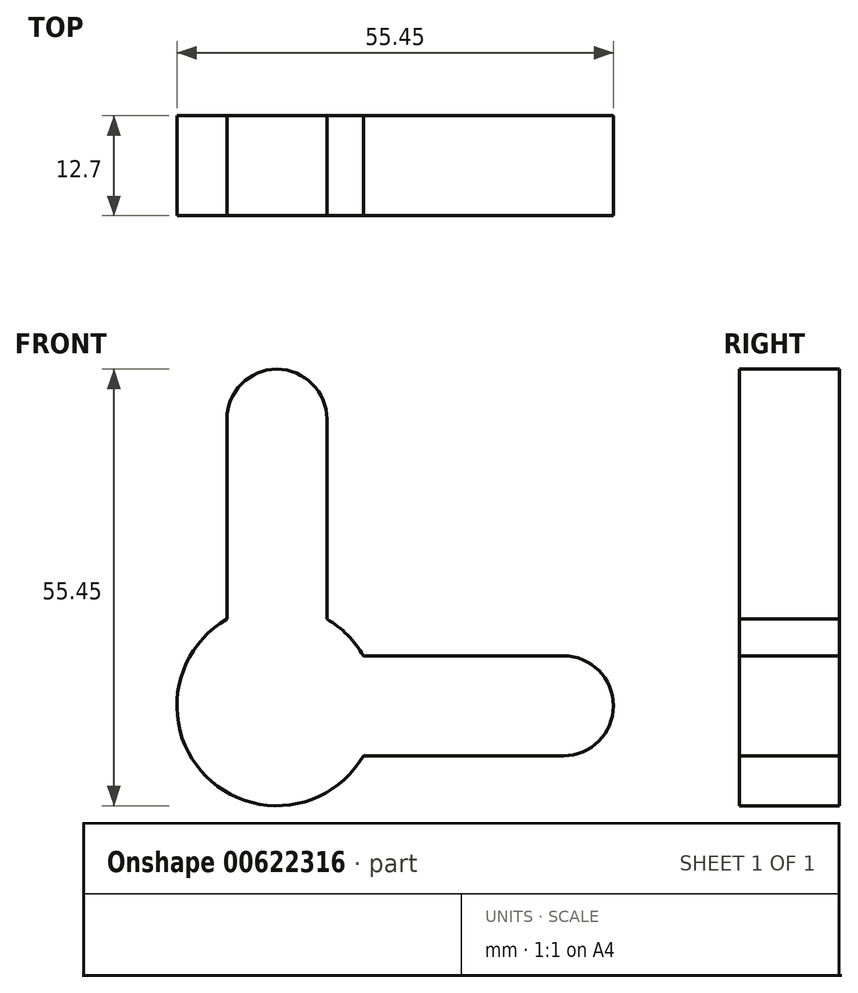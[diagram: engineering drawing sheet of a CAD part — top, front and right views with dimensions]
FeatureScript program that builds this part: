
annotation { "Feature Type Name" : "Feature", "Feature Type Description" : "" }
export const myFeature = defineFeature(function(context is Context, id is Id, definition is map)
    precondition{}
    {
        {
            var Q0;
            Q0=qCreatedBy(makeId("Front.planeOp"),FACE);
            var sketch = newSketch(context, id + "F0", { "sketchPlane" : qUnion([Q0])});
            skLineSegment(sketch, "E0", {"start": v(-6.35, 17.35) * mm, "end": v(-6.35, 42.75) * mm});
            skArc(sketch, "E1", {"start": v(6.35, 42.75) * mm, "mid": v(0, 49.1) * mm, "end": v(-6.35, 42.75) * mm});
            skLineSegment(sketch, "E2", {"start": v(6.35, 42.75) * mm, "end": v(6.35, 17.35) * mm});
            skCircle(sketch, "E3", {"center": v(0, 6.35) * mm, "radius": 12.7 * mm});
            skLineSegment(sketch, "E4", {"start": v(11, 12.7) * mm, "end": v(36.4, 12.7) * mm});
            skLineSegment(sketch, "E5", {"start": v(11, 0) * mm, "end": v(36.4, 0) * mm});
            skArc(sketch, "E6", {"start": v(36.4, 0) * mm, "mid": v(42.75, 6.35) * mm, "end": v(36.4, 12.7) * mm});
            skLineSegment(sketch, "E7", {"start": v(0, 6.35) * mm, "end": v(-90.28, 6.35) * mm, "construction": true});
            skLineSegment(sketch, "E8", {"start": v(0, 6.35) * mm, "end": v(0, -53.54) * mm, "construction": true});
            skArc(sketch, "E9.MirrorCS", {"start": v(-36.4, 0) * mm, "mid": v(-42.75, 6.35) * mm, "end": v(-36.4, 12.7) * mm});
            skLineSegment(sketch, "E10.MirrorCS", {"start": v(-11, 0) * mm, "end": v(-36.4, 0) * mm});
            skLineSegment(sketch, "E11.MirrorCS", {"start": v(-11, 12.7) * mm, "end": v(-36.4, 12.7) * mm});
            skArc(sketch, "E12.MirrorCS", {"start": v(6.35, -30.05) * mm, "mid": v(0, -36.4) * mm, "end": v(-6.35, -30.05) * mm});
            skLineSegment(sketch, "E13.MirrorCS", {"start": v(-6.35, -4.65) * mm, "end": v(-6.35, -30.05) * mm});
            skLineSegment(sketch, "E14.MirrorCS", {"start": v(6.35, -30.05) * mm, "end": v(6.35, -4.65) * mm});
            skSolve(sketch);
        }
        {
            var Q0;
            {var subQ0=sQuery(id+"F0.wireOp",EDGE,"E3");var subQ4=makeQuery(id+"F0.imprint","INTERSECT",VERTEX,{"derivedFrom":[sQuery(id+"F0.wireOp",EDGE,"E2"),subQ0]});Q0=makeQuery(id+"F0.imprint","IMPRINT",FACE,{"disambiguationData":[TD([[makeQuery(id+"F0.imprint","IMPRINT",EDGE,{"disambiguationData":[TD([[subQ4,1.0]])],"derivedFrom":subQ0}),1.0]])]});}
            var Q1;
            {var subQ0=sQuery(id+"F0.wireOp",EDGE,"E0");Q1=makeQuery(id+"F0.imprint","IMPRINT",FACE,{"disambiguationData":[TD([[makeQuery(id+"F0.imprint","IMPRINT",EDGE,{"derivedFrom":subQ0}),-1.0]])]});}
            var Q2;
            Q2=makeQuery(id+"F0.imprint","IMPRINT",FACE,{"disambiguationData":[TD([[makeQuery(id+"F0.imprint","IMPRINT",EDGE,{"derivedFrom":sQuery(id+"F0.wireOp",EDGE,"E9.MirrorCS")}),-1.0]])]});
            var Q3;
            {var subQ0=sQuery(id+"F0.wireOp",EDGE,"E4");Q3=makeQuery(id+"F0.imprint","IMPRINT",FACE,{"disambiguationData":[TD([[makeQuery(id+"F0.imprint","IMPRINT",EDGE,{"derivedFrom":subQ0}),-1.0]])]});}
            var Q4;
            Q4=makeQuery(id+"F0.imprint","IMPRINT",FACE,{"disambiguationData":[TD([[makeQuery(id+"F0.imprint","IMPRINT",EDGE,{"derivedFrom":sQuery(id+"F0.wireOp",EDGE,"E12.MirrorCS")}),-1.0]])]});
            extrude(context, id + "F1", {"entities" : qUnion([Q0, Q1, Q2, Q3, Q4]), "depth" : 12.7 * mm, "offsetDistance" : 25.4 * mm, "symmetric" : true});
        }
    });
